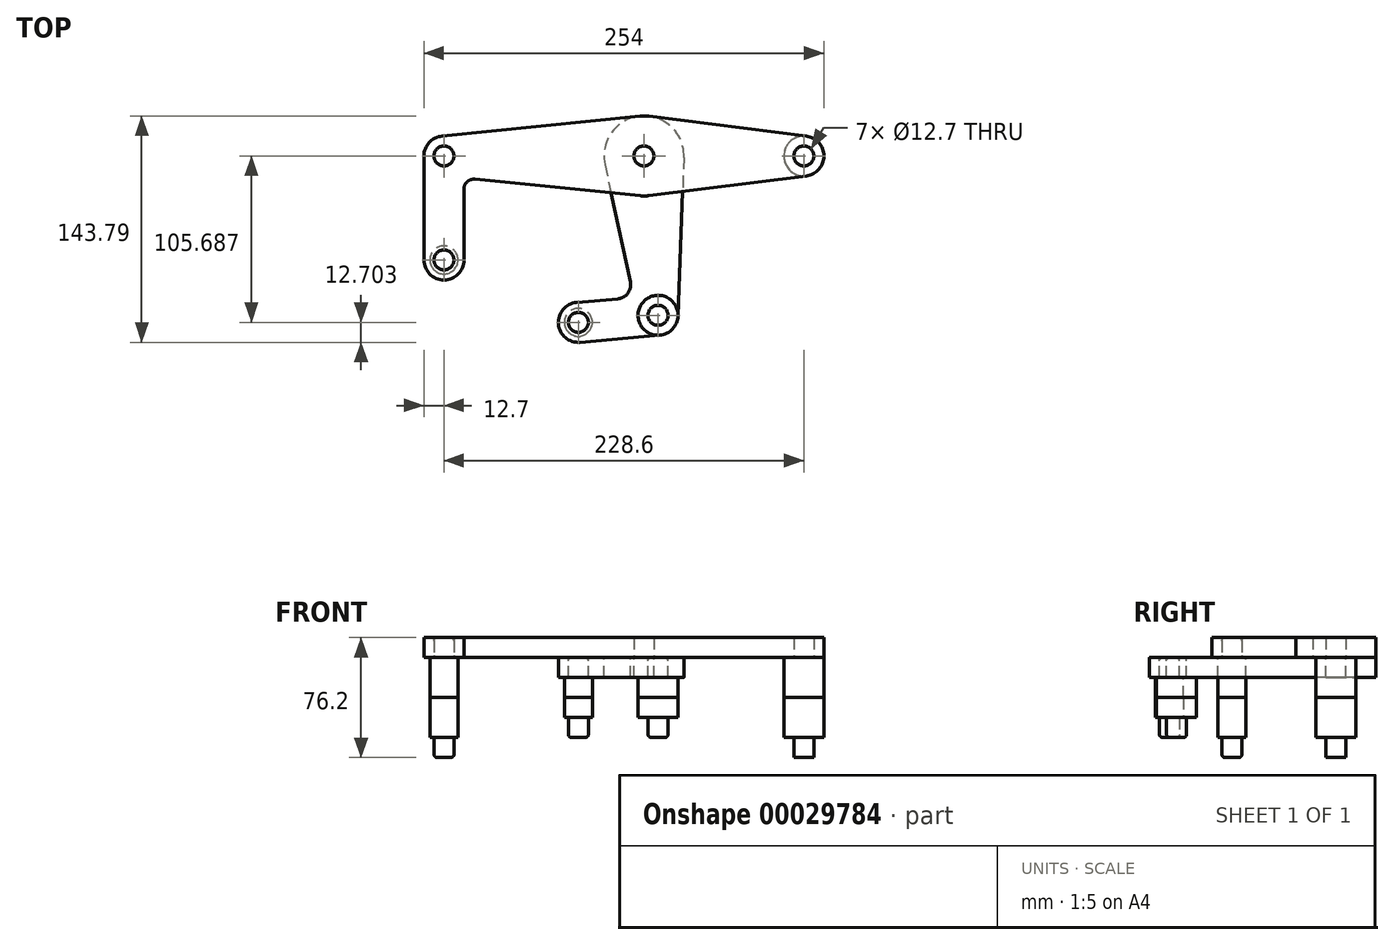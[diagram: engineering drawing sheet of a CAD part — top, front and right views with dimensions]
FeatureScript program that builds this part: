
annotation { "Feature Type Name" : "Feature", "Feature Type Description" : "" }
export const myFeature = defineFeature(function(context is Context, id is Id, definition is map)
    precondition{}
    {
        {
            var Q0;
            Q0=qCreatedBy(makeId("Top.planeOp"),FACE);
            var sketch = newSketch(context, id + "F0", { "sketchPlane" : qUnion([Q0])});
            skCircle(sketch, "E0", {"center": v(0, 0) * mm, "radius": 25.4 * mm});
            skLineSegment(sketch, "E1", {"start": v(0, 0) * mm, "end": v(101.6, 0) * mm, "construction": true});
            skCircle(sketch, "E2", {"center": v(101.6, 0) * mm, "radius": 12.7 * mm});
            skLineSegment(sketch, "E3", {"start": v(3.17, 25.2) * mm, "end": v(103.19, 12.6) * mm});
            skLineSegment(sketch, "E4.MirrorCS", {"start": v(3.17, -25.2) * mm, "end": v(103.19, -12.6) * mm});
            skLineSegment(sketch, "E5", {"start": v(0, 0) * mm, "end": v(8.97, -101.2) * mm, "construction": true});
            skLineSegment(sketch, "E6", {"start": v(8.97, -101.2) * mm, "end": v(-41.63, -105.69) * mm, "construction": true});
            skCircle(sketch, "E7", {"center": v(8.97, -101.2) * mm, "radius": 12.7 * mm});
            skLineSegment(sketch, "E8", {"start": v(25.38, -0.94) * mm, "end": v(21.66, -101.67) * mm});
            skLineSegment(sketch, "E9.MirrorCS", {"start": v(-24.82, -5.39) * mm, "end": v(-8.64, -79.97) * mm});
            skCircle(sketch, "E10", {"center": v(-41.63, -105.69) * mm, "radius": 12.7 * mm});
            skLineSegment(sketch, "E11", {"start": v(10.09, -113.85) * mm, "end": v(-40.51, -118.34) * mm});
            skLineSegment(sketch, "E12.MirrorCS", {"start": v(-16.54, -90.71) * mm, "end": v(-42.76, -93.04) * mm});
            skPoint(sketch, "E13.newPointA", {"position": v(7.85, -88.55) * mm});
            skPoint(sketch, "E13.newPointB", {"position": v(-3.44, -103.9) * mm});
            skArc(sketch, "E13.filletArc", {"start": v(-16.54, -90.71) * mm, "mid": v(-10.16, -87.13) * mm, "end": v(-8.64, -79.97) * mm});
            skCircle(sketch, "E14", {"center": v(-41.63, -105.69) * mm, "radius": 6.35 * mm});
            skCircle(sketch, "E15", {"center": v(8.97, -101.2) * mm, "radius": 6.35 * mm});
            skCircle(sketch, "E16", {"center": v(101.6, 0) * mm, "radius": 6.35 * mm});
            skCircle(sketch, "E17", {"center": v(0, 0) * mm, "radius": 6.35 * mm});
            skLineSegment(sketch, "E18", {"start": v(0, 0) * mm, "end": v(-127, 0) * mm, "construction": true});
            skCircle(sketch, "E19", {"center": v(-127, 0) * mm, "radius": 12.7 * mm});
            skCircle(sketch, "E20", {"center": v(-127, 0) * mm, "radius": 6.35 * mm});
            skLineSegment(sketch, "E21", {"start": v(-128.27, 12.64) * mm, "end": v(-2.54, 25.27) * mm});
            skLineSegment(sketch, "E22.MirrorCS", {"start": v(-107.32, -14.74) * mm, "end": v(-2.54, -25.27) * mm});
            skLineSegment(sketch, "E23", {"start": v(-127, 0) * mm, "end": v(-127, -66.04) * mm, "construction": true});
            skCircle(sketch, "E24", {"center": v(-127, -66.04) * mm, "radius": 12.7 * mm});
            skCircle(sketch, "E25", {"center": v(-127, -66.04) * mm, "radius": 6.35 * mm});
            skLineSegment(sketch, "E26", {"start": v(-139.7, 0) * mm, "end": v(-139.7, -66.04) * mm});
            skLineSegment(sketch, "E27.MirrorCS", {"start": v(-114.3, -21.06) * mm, "end": v(-114.3, -66.04) * mm});
            skPoint(sketch, "E28.newPointA", {"position": v(-128.27, -12.64) * mm});
            skPoint(sketch, "E28.newPointB", {"position": v(-114.3, 0) * mm});
            skArc(sketch, "E28.filletArc", {"start": v(-107.32, -14.74) * mm, "mid": v(-112.2, -16.35) * mm, "end": v(-114.3, -21.06) * mm});
            skSolve(sketch);
        }
        {
            var Q0;
            {var subQ7=sQuery(id+"F0.wireOp",EDGE,"E3");Q0=makeQuery(id+"F0.imprint","IMPRINT",FACE,{"disambiguationData":[TD([[makeQuery(id+"F0.imprint","IMPRINT",EDGE,{"derivedFrom":subQ7}),-1.0]])]});}
            var Q1;
            Q1=makeQuery(id+"F0.imprint","IMPRINT",FACE,{"disambiguationData":[TD([[makeQuery(id+"F0.imprint","IMPRINT",EDGE,{"derivedFrom":sQuery(id+"F0.wireOp",EDGE,"E16")}),-1.0]])]});
            var Q2;
            {var subQ1=sQuery(id+"F0.wireOp",EDGE,"E4.MirrorCS");var subQ3=sQuery(id+"F0.wireOp",EDGE,"E0");var subQ5=makeQuery(id+"F0.imprint","INTERSECT",VERTEX,{"derivedFrom":[subQ3,subQ1]});Q2=makeQuery(id+"F0.imprint","IMPRINT",FACE,{"disambiguationData":[TD([[makeQuery(id+"F0.imprint","IMPRINT",EDGE,{"disambiguationData":[TD([[subQ5,-1.0]])],"derivedFrom":subQ3}),-1.0]])]});}
            var Q3;
            Q3=makeQuery(id+"F0.imprint","IMPRINT",FACE,{"disambiguationData":[TD([[makeQuery(id+"F0.imprint","IMPRINT",EDGE,{"derivedFrom":sQuery(id+"F0.wireOp",EDGE,"E17")}),-1.0]])]});
            var Q4;
            {var subQ1=sQuery(id+"F0.wireOp",EDGE,"E9.MirrorCS");var subQ3=sQuery(id+"F0.wireOp",EDGE,"E0");var subQ5=makeQuery(id+"F0.imprint","INTERSECT",VERTEX,{"derivedFrom":[subQ3,subQ1]});Q4=makeQuery(id+"F0.imprint","IMPRINT",FACE,{"disambiguationData":[TD([[makeQuery(id+"F0.imprint","IMPRINT",EDGE,{"disambiguationData":[TD([[subQ5,-1.0]])],"derivedFrom":subQ3}),-1.0]])]});}
            var Q5;
            {var subQ7=sQuery(id+"F0.wireOp",EDGE,"E21");Q5=makeQuery(id+"F0.imprint","IMPRINT",FACE,{"disambiguationData":[TD([[makeQuery(id+"F0.imprint","IMPRINT",EDGE,{"derivedFrom":subQ7}),-1.0]])]});}
            var Q6;
            Q6=makeQuery(id+"F0.imprint","IMPRINT",FACE,{"disambiguationData":[TD([[makeQuery(id+"F0.imprint","IMPRINT",EDGE,{"derivedFrom":sQuery(id+"F0.wireOp",EDGE,"E20")}),-1.0]])]});
            var Q7;
            Q7=makeQuery(id+"F0.imprint","IMPRINT",FACE,{"disambiguationData":[TD([[makeQuery(id+"F0.imprint","IMPRINT",EDGE,{"derivedFrom":sQuery(id+"F0.wireOp",EDGE,"E25")}),-1.0]])]});
            extrude(context, id + "F1", {"entities" : qUnion([Q0, Q1, Q2, Q3, Q4, Q5, Q6, Q7]), "depth" : 12.7 * mm});
        }
        {
            var Q0;
            Q0=makeQuery(id+"F0.imprint","IMPRINT",FACE,{"disambiguationData":[TD([[makeQuery(id+"F0.imprint","IMPRINT",EDGE,{"derivedFrom":sQuery(id+"F0.wireOp",EDGE,"E14")}),-1.0]])]});
            var Q1;
            {var subQ6=sQuery(id+"F0.wireOp",EDGE,"E11");Q1=makeQuery(id+"F0.imprint","IMPRINT",FACE,{"disambiguationData":[TD([[makeQuery(id+"F0.imprint","IMPRINT",EDGE,{"derivedFrom":subQ6}),-1.0]])]});}
            var Q2;
            Q2=makeQuery(id+"F0.imprint","IMPRINT",FACE,{"disambiguationData":[TD([[makeQuery(id+"F0.imprint","IMPRINT",EDGE,{"derivedFrom":sQuery(id+"F0.wireOp",EDGE,"E15")}),-1.0]])]});
            var Q3;
            {var subQ1=sQuery(id+"F0.wireOp",EDGE,"E4.MirrorCS");var subQ3=sQuery(id+"F0.wireOp",EDGE,"E0");var subQ5=makeQuery(id+"F0.imprint","INTERSECT",VERTEX,{"derivedFrom":[subQ3,subQ1]});Q3=makeQuery(id+"F0.imprint","IMPRINT",FACE,{"disambiguationData":[TD([[makeQuery(id+"F0.imprint","IMPRINT",EDGE,{"disambiguationData":[TD([[subQ5,-1.0]])],"derivedFrom":subQ3}),-1.0]])]});}
            var Q4;
            Q4=makeQuery(id+"F0.imprint","IMPRINT",FACE,{"disambiguationData":[TD([[makeQuery(id+"F0.imprint","IMPRINT",EDGE,{"derivedFrom":sQuery(id+"F0.wireOp",EDGE,"E17")}),-1.0]])]});
            var Q5;
            {var subQ1=sQuery(id+"F0.wireOp",EDGE,"E9.MirrorCS");var subQ3=sQuery(id+"F0.wireOp",EDGE,"E0");var subQ5=makeQuery(id+"F0.imprint","INTERSECT",VERTEX,{"derivedFrom":[subQ3,subQ1]});Q5=makeQuery(id+"F0.imprint","IMPRINT",FACE,{"disambiguationData":[TD([[makeQuery(id+"F0.imprint","IMPRINT",EDGE,{"disambiguationData":[TD([[subQ5,-1.0]])],"derivedFrom":subQ3}),-1.0]])]});}
            extrude(context, id + "F2", {"entities" : qUnion([Q0, Q1, Q2, Q3, Q4, Q5]), "oppositeDirection" : true, "depth" : 12.7 * mm});
        }
        {
            var Q0;
            Q0=makeQuery(id+"F1.opExtrude","CAP_FACE",FACE,{"disambiguationData":[OSD([sQuery(id+"F0.wireOp",EDGE,"E0"),sQuery(id+"F0.wireOp",EDGE,"E2"),sQuery(id+"F0.wireOp",EDGE,"E3"),sQuery(id+"F0.wireOp",EDGE,"E4.MirrorCS"),sQuery(id+"F0.wireOp",EDGE,"E16"),sQuery(id+"F0.wireOp",EDGE,"E17"),sQuery(id+"F0.wireOp",EDGE,"E19"),sQuery(id+"F0.wireOp",EDGE,"E20"),sQuery(id+"F0.wireOp",EDGE,"E21"),sQuery(id+"F0.wireOp",EDGE,"E22.MirrorCS"),sQuery(id+"F0.wireOp",EDGE,"E24"),sQuery(id+"F0.wireOp",EDGE,"E25"),sQuery(id+"F0.wireOp",EDGE,"E26"),sQuery(id+"F0.wireOp",EDGE,"E27.MirrorCS"),sQuery(id+"F0.wireOp",EDGE,"E28.filletArc")])],"isStart":false});
            var sketch = newSketch(context, id + "F3", { "sketchPlane" : qUnion([Q0])});
            skCircle(sketch, "E29", {"center": v(101.6, 0) * mm, "radius": 12.7 * mm});
            skCircle(sketch, "E30", {"center": v(-127, -66.04) * mm, "radius": 8.9 * mm});
            skSolve(sketch);
        }
        {
            var Q0;
            Q0=makeQuery(id+"F2.opExtrude","CAP_FACE",FACE,{"disambiguationData":[OSD([sQuery(id+"F0.wireOp",EDGE,"E0"),sQuery(id+"F0.wireOp",EDGE,"E7"),sQuery(id+"F0.wireOp",EDGE,"E9.MirrorCS"),sQuery(id+"F0.wireOp",EDGE,"E8"),sQuery(id+"F0.wireOp",EDGE,"E10"),sQuery(id+"F0.wireOp",EDGE,"E11"),sQuery(id+"F0.wireOp",EDGE,"E12.MirrorCS"),sQuery(id+"F0.wireOp",EDGE,"E13.filletArc"),sQuery(id+"F0.wireOp",EDGE,"E14"),sQuery(id+"F0.wireOp",EDGE,"E15"),sQuery(id+"F0.wireOp",EDGE,"E17")])],"isStart":true});
            var sketch = newSketch(context, id + "F4", { "sketchPlane" : qUnion([Q0])});
            skCircle(sketch, "E31", {"center": v(8.97, -101.2) * mm, "radius": 12.7 * mm});
            skCircle(sketch, "E32", {"center": v(-41.63, -105.69) * mm, "radius": 8.9 * mm});
            skSolve(sketch);
        }
        {
            var Q0;
            Q0=makeQuery(id+"F2.opExtrude","CAP_FACE",FACE,{"disambiguationData":[OSD([sQuery(id+"F0.wireOp",EDGE,"E0"),sQuery(id+"F0.wireOp",EDGE,"E7"),sQuery(id+"F0.wireOp",EDGE,"E9.MirrorCS"),sQuery(id+"F0.wireOp",EDGE,"E8"),sQuery(id+"F0.wireOp",EDGE,"E10"),sQuery(id+"F0.wireOp",EDGE,"E11"),sQuery(id+"F0.wireOp",EDGE,"E12.MirrorCS"),sQuery(id+"F0.wireOp",EDGE,"E13.filletArc"),sQuery(id+"F0.wireOp",EDGE,"E14"),sQuery(id+"F0.wireOp",EDGE,"E15"),sQuery(id+"F0.wireOp",EDGE,"E17")])],"isStart":false});
            cPlane(context, id + "F5", {"entities" : qUnion([Q0]), "cplaneType" : CPlaneType.OFFSET, "offset" : 12.7 * mm, "width" : 152.4 * mm, "height" : 152.4 * mm});
        }
        {
            var Q0;
            Q0 = qSketchRegion(id + "F3", true);
            var Q1;
            Q1 = qSketchRegion(id + "F4", true);
            var Q2;
            Q2=qCreatedBy(id+"F5.planeOp",FACE);
            extrude(context, id + "F6", {"entities" : qUnion([Q0, Q1]), "endBound" : BoundingType.UP_TO_SURFACE, "oppositeDirection" : true, "endBoundEntityFace" : qUnion([Q2]), "depth" : 25.4 * mm});
        }
        {
            var Q0;
            Q0=makeQuery(id+"F1.opExtrude","SWEPT_BODY",BODY,{"disambiguationData":[OSD([sQuery(id+"F0.wireOp",EDGE,"E0"),sQuery(id+"F0.wireOp",EDGE,"E2"),sQuery(id+"F0.wireOp",EDGE,"E3"),sQuery(id+"F0.wireOp",EDGE,"E4.MirrorCS"),sQuery(id+"F0.wireOp",EDGE,"E16"),sQuery(id+"F0.wireOp",EDGE,"E17"),sQuery(id+"F0.wireOp",EDGE,"E19"),sQuery(id+"F0.wireOp",EDGE,"E20"),sQuery(id+"F0.wireOp",EDGE,"E21"),sQuery(id+"F0.wireOp",EDGE,"E22.MirrorCS"),sQuery(id+"F0.wireOp",EDGE,"E24"),sQuery(id+"F0.wireOp",EDGE,"E25"),sQuery(id+"F0.wireOp",EDGE,"E26"),sQuery(id+"F0.wireOp",EDGE,"E27.MirrorCS"),sQuery(id+"F0.wireOp",EDGE,"E28.filletArc")])]});
            var Q1;
            Q1=makeQuery(id+"F2.opExtrude","SWEPT_BODY",BODY,{"disambiguationData":[OSD([sQuery(id+"F0.wireOp",EDGE,"E0"),sQuery(id+"F0.wireOp",EDGE,"E7"),sQuery(id+"F0.wireOp",EDGE,"E9.MirrorCS"),sQuery(id+"F0.wireOp",EDGE,"E8"),sQuery(id+"F0.wireOp",EDGE,"E10"),sQuery(id+"F0.wireOp",EDGE,"E11"),sQuery(id+"F0.wireOp",EDGE,"E12.MirrorCS"),sQuery(id+"F0.wireOp",EDGE,"E13.filletArc"),sQuery(id+"F0.wireOp",EDGE,"E14"),sQuery(id+"F0.wireOp",EDGE,"E15"),sQuery(id+"F0.wireOp",EDGE,"E17")])]});
            var Q2;
            Q2=makeQuery(id+"F6.opExtrude","SWEPT_BODY",BODY,{"disambiguationData":[OSD([sQuery(id+"F3.wireOp",EDGE,"E29")])]});
            var Q3;
            Q3=makeQuery(id+"F6.opExtrude","SWEPT_BODY",BODY,{"disambiguationData":[OSD([sQuery(id+"F3.wireOp",EDGE,"E30")])]});
            var Q4;
            Q4=makeQuery(id+"F6.opExtrude","SWEPT_BODY",BODY,{"disambiguationData":[OSD([sQuery(id+"F4.wireOp",EDGE,"E31")])]});
            var Q5;
            Q5=makeQuery(id+"F6.opExtrude","SWEPT_BODY",BODY,{"disambiguationData":[OSD([sQuery(id+"F4.wireOp",EDGE,"E32")])]});
            booleanBodies(context, id + "F7", {"operationType" : BooleanOperationType.SUBTRACTION, "tools" : qUnion([Q0, Q1]), "targets" : qUnion([Q2, Q3, Q4, Q5]), "keepTools" : true});
        }
        {
            var Q0;
            Q0=makeQuery(id+"F6.opExtrude","CAP_FACE",FACE,{"disambiguationData":[OSD([sQuery(id+"F3.wireOp",EDGE,"E30")])],"isStart":true});
            var Q1;
            Q1=makeQuery(id+"F6.opExtrude","CAP_FACE",FACE,{"disambiguationData":[OSD([sQuery(id+"F4.wireOp",EDGE,"E32")])],"isStart":true});
            var Q2;
            Q2=makeQuery(id+"F6.opExtrude","CAP_FACE",FACE,{"disambiguationData":[OSD([sQuery(id+"F4.wireOp",EDGE,"E31")])],"isStart":true});
            var Q3;
            Q3=makeQuery(id+"F7.opBoolean","COPY",EDGE,{"derivedFrom":makeQuery(id+"F1.opExtrude","CAP_EDGE",EDGE,{"disambiguationData":[OSD([sQuery(id+"F0.wireOp",EDGE,"E16")])],"isStart":false})});
            fillet(context, id + "F8", {"entities" : qUnion([Q0, Q1, Q2, Q3]), "radius" : 2.03 * mm, "tangentPropagation" : true, "allowEdgeOverflow" : false});
        }
        {
            var Q0;
            Q0=makeQuery(id+"F6.opExtrude","SWEPT_BODY",BODY,{"disambiguationData":[OSD([sQuery(id+"F3.wireOp",EDGE,"E29")])]});
            var Q1;
            Q1=makeQuery(id+"F6.opExtrude","SWEPT_BODY",BODY,{"disambiguationData":[OSD([sQuery(id+"F3.wireOp",EDGE,"E30")])]});
            var Q2;
            Q2=makeQuery(id+"F6.opExtrude","SWEPT_BODY",BODY,{"disambiguationData":[OSD([sQuery(id+"F4.wireOp",EDGE,"E31")])]});
            var Q3;
            Q3=makeQuery(id+"F6.opExtrude","SWEPT_BODY",BODY,{"disambiguationData":[OSD([sQuery(id+"F4.wireOp",EDGE,"E32")])]});
            var Q4;
            Q4=qCreatedBy(id+"F5.planeOp",FACE);
            mirror(context, id + "F9", {"entities" : qUnion([Q0, Q1, Q2, Q3]), "mirrorPlane" : qUnion([Q4])});
        }
    });
